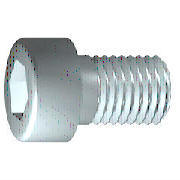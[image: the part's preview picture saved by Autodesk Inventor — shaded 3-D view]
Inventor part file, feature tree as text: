
AUTODESK INVENTOR PART (.ipt)
format: ipt  version: 2018 (Build 220112000, 112)  size: 187,392 bytes
history: native  units: mm (DEFAULTED — no unit token found)
features: sketch x2, extrude x1, plane x1, fillet x1
ambient origin geometry x7: Origin, YZ Plane, XY Plane, X Axis, Y Axis, Z Axis, Center Point
bodies: Solid1 (feature_tree), Body (feature_tree)
feature tree (5):
  extrude  "Slot"  Depth=3.0mm
  plane  "Work Plane1"
  fillet  "Fillet2"  Radius=3.0mm
  sketch  "Sketch1"  dims[d1=14.693275mm d2=0.306825mm d3=3.0mm]
  sketch  "Sketch2"  dims[d4=1.5mm d5=60.0deg d6=3.0mm d7=3.0mm d8=2.886751mm d9=5.5mm d10=90.0deg d11=10.0mm d12=0.0mm d13=14.693275mm d14=0.0mm d15=0.306725mm d16=0.306725mm d17=0.3mm d19=0.0mm d26=16.0mm d27=45.0deg d28=0.0mm d29=0.0mm d30=0.1mm]
